# Revit family: Gira_207712
name_source: partatom
category: Elektroinstallationen
revit_build: Autodesk Revit 2017 (Build: 20160225_1515(x64)
units: mm (PartAtom-declared; Revit-internal decimal feet)

## family parameters
Basisbauteil = Fläche
Beim Laden mit Abzugskörper schneiden = Nein
Bemaßung runder Anschluss = Durchmesser verwenden
Beschriftungsausrichtung beibehalten = Nein
Gemeinsam genutzt = Nein
Raumberechnungspunkt = Nein
Teiletyp = Normal

## types (1)
- Gira_207712
    BIM = https://media.stage.bim.site X1 REG KNX.rfa
    Beschreibung = Gira G1 24V G1 GWh,Gira G1 24 V,,white glass,The Gira G1 is a multi-functional room operating device for visualising and operating a variety of building functions. For use in the KNX system and Gira door communication system, or as client. The respective range of functions depends on the firmware used., , When used as a client, the KNX room operating device features are not available. For details on the exact scope of functions, please refer to the Gira online catalogue and the device's technical documentation.,,Features:,- Operation is via a gesture-capable multi-touch display.,- Connection and communication are via LAN or WLAN, depending on the variant.,- Integrated speaker.,- Integrated microphone with echo compensation.,  ,Potential applications and combinations:,- As a multi-functional room operating device, the Gira G1 offers the following functions and function combinations:,- KNX room operating device,- Home station video,- Integrates Internet services or as client for the following systems servers - HomeServer - eNet - X1 - Alarm Connect security system,Properties as a KNX room operating device:,- Intuitive user interface that can be adapted by the end user.,- Switching and dimming (relative and absolute), dimming (incl. Dimming RGB, RGBW, and Tunable White), blind and roller shutter control, value transmitter, and scene auxiliary unit.,- Status display, display of date and time, display of indoor and outdoor temperature.,- Up to 150 functions (six function folders or rooms with up to 25 functions each).,- Up to 125 seven-day timer with 10 switching times each.,- Room temperature controller in combination with the temperature sensor module (available as an optional extra), or KNX devices for room temperature measurement, e.g. touch sensor 3 Komfort.,- Operating modes: Comfort, standby, night, and frost or heat protection with their own temperature setpoint values (for heating and or cooling).,- Operating modes can be adapted individually.,- A heating clock as seven-day timer with 28 switching times.,- Room temperature controller auxiliary unit for controlling air conditioning systems (fan coil) in conjunction with a KNX gateway for air conditioning systems.,Properties as video home station:,- Camera changeover: specific selection of connected colour cameras. ,- Control of the door opener.,- Switching the ringtone on and off.,- Ring tone can be selected from a choice of 10 melodies.,- Internal calls.,Integration of Internet services:,- Gira weather service: display of the weather forecast for up to five cities (internet connection required).,Gira G1 can also be used as a client for the following systems servers (requires firmware update)::,- HomeServer Client,- eNet Client,- X1 Client,- Gira G1 with flush-mounted connection module 24 V WLAN for connecting to a suitable cable (e.g. to the second wire pair of the KNX bus line).,- Data communication via WLAN.,,Notes :,- Suitable for indoor use only.,- Recommended mounting height: 150 cm above floor.,- Installation is performed on a deep device box (an electronics box is recommended for a LAN connection).,- Communication with the KNX installation is exclusively via the KNXnet IP standard.,- A KNX IP router must be used to connect the Gira G1 PoE to the KNX installation. Several Gira G1 units can be operated on one KNX IP router.,- In order to ensure reliable communication via WLAN, a Gira KNX IP router (firmware version 3 and later) is required to connect the Gira G1 230 V or G1 24 V to the KNX installation. For this purpose the Gira KNX IP router (firmware version 3 and later) is specially equipped with the additional function Reliable data communication". Several Gira G1 units can be operated on one Gira KNX IP router (firmware version 3 and later).,- Hardware from index status I08 prepared for KNX Secure (additional firmware update required).,- Commissioning in the KNX system from ETS 5.5 or higher.,- Can be used as a home station in connection with the DCS-IP gateway.,- When planning the system, please observe the technical information on network planning in the device documentation.,- The Gira Project Assistant (GPA) is required for firmware updates. The GPA is available free of charge in the Gira download area.,- Using the timers requires either an internet connection to a NTP time server or a KNX clock (e.g. Gira weather station Plus 2074 00).,- When used as a Gira HomeServer client, the Gira G1's temperature sensor module is not supported.,- For dimensioning the power supply, the total power consumption of all connected devices as well as the voltage drop in the supply network must always be considered."
    Bus connection included = Nein
    Bus system KNX = Ja
    Bus system KNX radio = Nein
    Bus system LON = Nein
    Bus system Powernet = Nein
    Bus system radio frequent = Nein
    Central functional unit for senders/actuators = Ja
    Data sheet = https://katalog.gira.de
    Degree of protection (IP) = IP21
    GTIN = 4010337014317
    HAN = 207712
    Hersteller = Gira
    IR sensor = Nein
    Integrated DCF77 receiver = Nein
    Material = Other
    Material quality = Other
    Mounting method = Flush mounted (plaster)
    Other bus systems = None
    Presence button = Nein
    Productwebsite = http://katalog.gira.de
    Status-LED = Ja
    Surface finishing = Not applicable
    Surface protection = Other
    Temperature controller = Ja
    Transparent = Nein
    Typname = Gira G1 24 V Gira G1 white gl.
    URL = https://www.gira.de
    Vorgabe-Ansicht = 1219 mm
    With anti-theft/dismantling protection = Ja
    With display = Ja

## geometry (parser evidence)
native form markers: Sweep x2
no freeform markers — native parametric forms only
